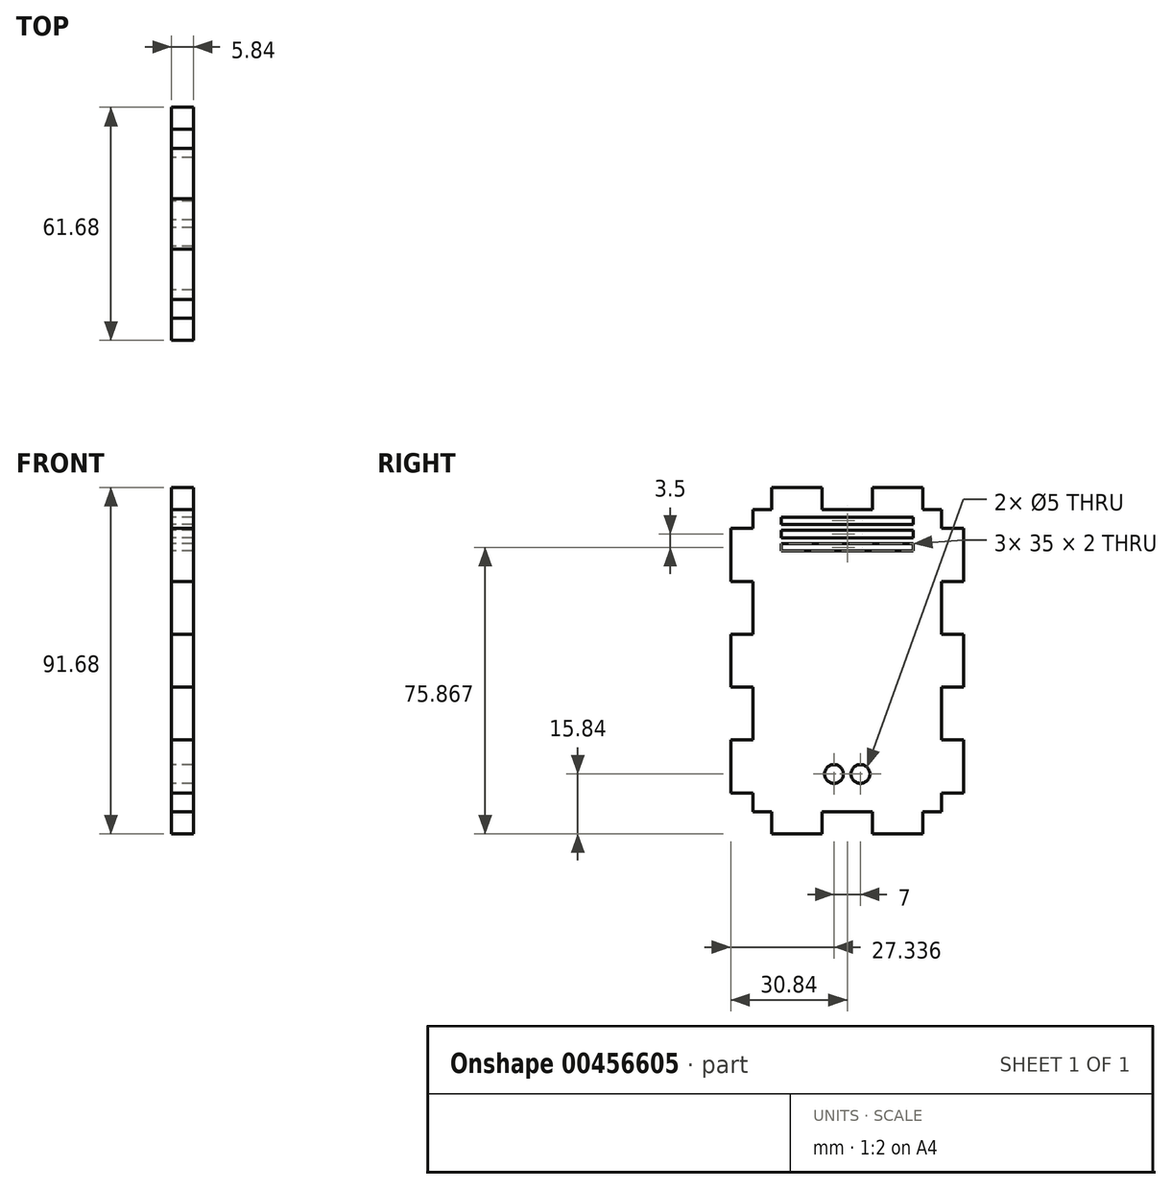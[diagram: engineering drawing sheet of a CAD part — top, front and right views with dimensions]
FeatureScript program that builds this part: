
annotation { "Feature Type Name" : "Feature", "Feature Type Description" : "" }
export const myFeature = defineFeature(function(context is Context, id is Id, definition is map)
    precondition{}
    {
        {
            var Q0;
            Q0=qCreatedBy(makeId("Right.planeOp"),FACE);
            var sketch = newSketch(context, id + "F0", { "sketchPlane" : qUnion([Q0])});
            skLineSegment(sketch, "E0.bottom", {"start": v(-25, -40) * mm, "end": v(-20, -40) * mm});
            skLineSegment(sketch, "E0.top", {"start": v(-25, 40) * mm, "end": v(-20, 40) * mm});
            skLineSegment(sketch, "E0.left", {"start": v(-25, -40) * mm, "end": v(-25, -35) * mm});
            skLineSegment(sketch, "E0.right", {"start": v(25, -40) * mm, "end": v(25, -35) * mm});
            skLineSegment(sketch, "E1.bottom", {"start": v(-20, 45.84) * mm, "end": v(-6.67, 45.84) * mm});
            skLineSegment(sketch, "E1.top", {"start": v(-20, -45.84) * mm, "end": v(-6.67, -45.84) * mm});
            skLineSegment(sketch, "E1.left", {"start": v(-30.84, 35) * mm, "end": v(-30.84, 21) * mm});
            skLineSegment(sketch, "E1.right", {"start": v(30.84, 35) * mm, "end": v(30.84, 21) * mm});
            skLineSegment(sketch, "E2.top", {"start": v(-30.84, 35) * mm, "end": v(-25, 35) * mm});
            skLineSegment(sketch, "E2.right", {"start": v(-20, 45.84) * mm, "end": v(-20, 40) * mm});
            skLineSegment(sketch, "E3.top", {"start": v(30.84, 35) * mm, "end": v(25, 35) * mm});
            skLineSegment(sketch, "E3.right", {"start": v(20, 45.84) * mm, "end": v(20, 40) * mm});
            skLineSegment(sketch, "E4.bottom", {"start": v(-6.67, 40) * mm, "end": v(6.67, 40) * mm});
            skLineSegment(sketch, "E4.left", {"start": v(-6.67, 40) * mm, "end": v(-6.67, 45.84) * mm});
            skLineSegment(sketch, "E4.right", {"start": v(6.67, 40) * mm, "end": v(6.67, 45.84) * mm});
            skLineSegment(sketch, "E5.top", {"start": v(-30.84, -35) * mm, "end": v(-25, -35) * mm});
            skLineSegment(sketch, "E5.right", {"start": v(-20, -45.84) * mm, "end": v(-20, -40) * mm});
            skLineSegment(sketch, "E6.top", {"start": v(30.84, -35) * mm, "end": v(25, -35) * mm});
            skLineSegment(sketch, "E6.right", {"start": v(20, -45.84) * mm, "end": v(20, -40) * mm});
            skLineSegment(sketch, "E7.top", {"start": v(-6.67, -40) * mm, "end": v(6.67, -40) * mm});
            skLineSegment(sketch, "E7.left", {"start": v(-6.67, -45.84) * mm, "end": v(-6.67, -40) * mm});
            skLineSegment(sketch, "E7.right", {"start": v(6.67, -45.84) * mm, "end": v(6.67, -40) * mm});
            skLineSegment(sketch, "E8.bottom", {"start": v(-30.84, 21) * mm, "end": v(-25, 21) * mm});
            skLineSegment(sketch, "E8.top", {"start": v(-30.84, 7) * mm, "end": v(-25, 7) * mm});
            skLineSegment(sketch, "E8.right", {"start": v(-25, 21) * mm, "end": v(-25, 7) * mm});
            skLineSegment(sketch, "E9.bottom", {"start": v(-30.84, -7) * mm, "end": v(-25, -7) * mm});
            skLineSegment(sketch, "E9.top", {"start": v(-30.84, -21) * mm, "end": v(-25, -21) * mm});
            skLineSegment(sketch, "E9.right", {"start": v(-25, -7) * mm, "end": v(-25, -21) * mm});
            skLineSegment(sketch, "E10.bottom", {"start": v(25, 21) * mm, "end": v(30.84, 21) * mm});
            skLineSegment(sketch, "E10.top", {"start": v(25, 7) * mm, "end": v(30.84, 7) * mm});
            skLineSegment(sketch, "E10.left", {"start": v(25, 21) * mm, "end": v(25, 7) * mm});
            skLineSegment(sketch, "E11.bottom", {"start": v(25, -7) * mm, "end": v(30.84, -7) * mm});
            skLineSegment(sketch, "E11.top", {"start": v(25, -21) * mm, "end": v(30.84, -21) * mm});
            skLineSegment(sketch, "E11.left", {"start": v(25, -7) * mm, "end": v(25, -21) * mm});
            skLineSegment(sketch, "E12.trimOffspring", {"start": v(6.67, 45.84) * mm, "end": v(20, 45.84) * mm});
            skLineSegment(sketch, "E13.trimOffspring", {"start": v(30.84, 7) * mm, "end": v(30.84, -7) * mm});
            skLineSegment(sketch, "E14.trimOffspring", {"start": v(30.84, -21) * mm, "end": v(30.84, -35) * mm});
            skLineSegment(sketch, "E15.trimOffspring", {"start": v(-30.84, 7) * mm, "end": v(-30.84, -7) * mm});
            skLineSegment(sketch, "E16.trimOffspring", {"start": v(-25, 35) * mm, "end": v(-25, 40) * mm});
            skLineSegment(sketch, "E17.trimOffspring", {"start": v(25, 35) * mm, "end": v(25, 40) * mm});
            skLineSegment(sketch, "E18.trimOffspring", {"start": v(20, 40) * mm, "end": v(25, 40) * mm});
            skLineSegment(sketch, "E19.trimOffspring", {"start": v(-25, 7) * mm, "end": v(-25, 21) * mm});
            skLineSegment(sketch, "E20.trimOffspring", {"start": v(-30.84, -21) * mm, "end": v(-30.84, -35) * mm});
            skLineSegment(sketch, "E21.trimOffspring", {"start": v(6.67, -45.84) * mm, "end": v(20, -45.84) * mm});
            skLineSegment(sketch, "E22.trimOffspring", {"start": v(25, 7) * mm, "end": v(25, 21) * mm});
            skLineSegment(sketch, "E23.trimOffspring", {"start": v(25, -21) * mm, "end": v(25, -7) * mm});
            skLineSegment(sketch, "E24.trimOffspring", {"start": v(-25, -21) * mm, "end": v(-25, -7) * mm});
            skLineSegment(sketch, "E25.trimOffspring", {"start": v(20, -40) * mm, "end": v(25, -40) * mm});
            skCircle(sketch, "E26", {"center": v(3.5, -30) * mm, "radius": 2.5 * mm});
            skCircle(sketch, "E27", {"center": v(-3.5, -30) * mm, "radius": 2.5 * mm});
            skLineSegment(sketch, "E28.bottom", {"start": v(17.5, 38.03) * mm, "end": v(-17.5, 38.03) * mm});
            skLineSegment(sketch, "E28.top", {"start": v(17.5, 36.03) * mm, "end": v(-17.5, 36.03) * mm});
            skLineSegment(sketch, "E28.left", {"start": v(17.5, 38.03) * mm, "end": v(17.5, 36.03) * mm});
            skLineSegment(sketch, "E28.right", {"start": v(-17.5, 38.03) * mm, "end": v(-17.5, 36.03) * mm});
            skPoint(sketch, "E28.middle", {"position": v(0, 37.03) * mm});
            skLineSegment(sketch, "E29.bottom", {"start": v(17.5, 34.53) * mm, "end": v(-17.5, 34.53) * mm});
            skLineSegment(sketch, "E29.top", {"start": v(17.5, 32.53) * mm, "end": v(-17.5, 32.53) * mm});
            skLineSegment(sketch, "E29.left", {"start": v(17.5, 34.53) * mm, "end": v(17.5, 32.53) * mm});
            skLineSegment(sketch, "E29.right", {"start": v(-17.5, 34.53) * mm, "end": v(-17.5, 32.53) * mm});
            skPoint(sketch, "E29.middle", {"position": v(0, 33.53) * mm});
            skLineSegment(sketch, "E30.bottom", {"start": v(17.5, 31.03) * mm, "end": v(-17.5, 31.03) * mm});
            skLineSegment(sketch, "E30.top", {"start": v(17.5, 29.03) * mm, "end": v(-17.5, 29.03) * mm});
            skLineSegment(sketch, "E30.left", {"start": v(17.5, 31.03) * mm, "end": v(17.5, 29.03) * mm});
            skLineSegment(sketch, "E30.right", {"start": v(-17.5, 31.03) * mm, "end": v(-17.5, 29.03) * mm});
            skPoint(sketch, "E30.middle", {"position": v(0, 30.03) * mm});
            skSolve(sketch);
        }
        {
            var Q0;
            Q0 = qSketchRegion(id + "F0", true);
            extrude(context, id + "F1", {"entities" : qUnion([Q0]), "depth" : 5.84 * mm});
        }
    });
